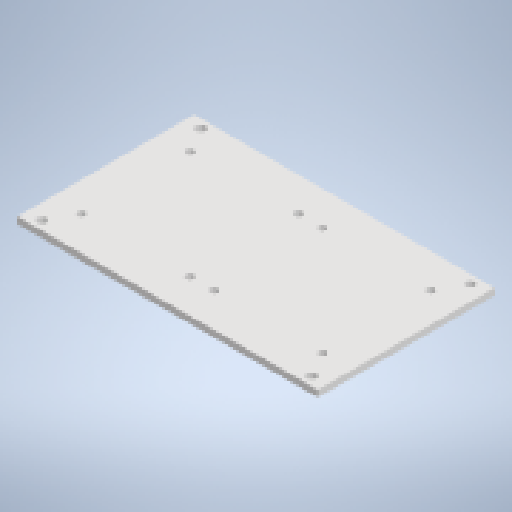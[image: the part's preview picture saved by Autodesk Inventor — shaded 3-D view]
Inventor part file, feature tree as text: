
AUTODESK INVENTOR PART (.ipt)
format: ipt  version: 2024 (Build 280153000, 153)  size: 173,056 bytes
history: native  units: mm
features: extrude x2, sketch x2, other x1
ambient origin geometry x8: Origin, YZ Plane, XZ Plane, XY Plane, X Axis, Y Axis, Z Axis, Center Point
bodies: Body1 (feature_tree)
feature tree (5):
  other  "솔리드1"
  extrude  "돌출1"  Depth=136.0mm
  extrude  "돌출2"  Depth=80.0mm
  sketch  "스케치1"
  sketch  "스케치2"
